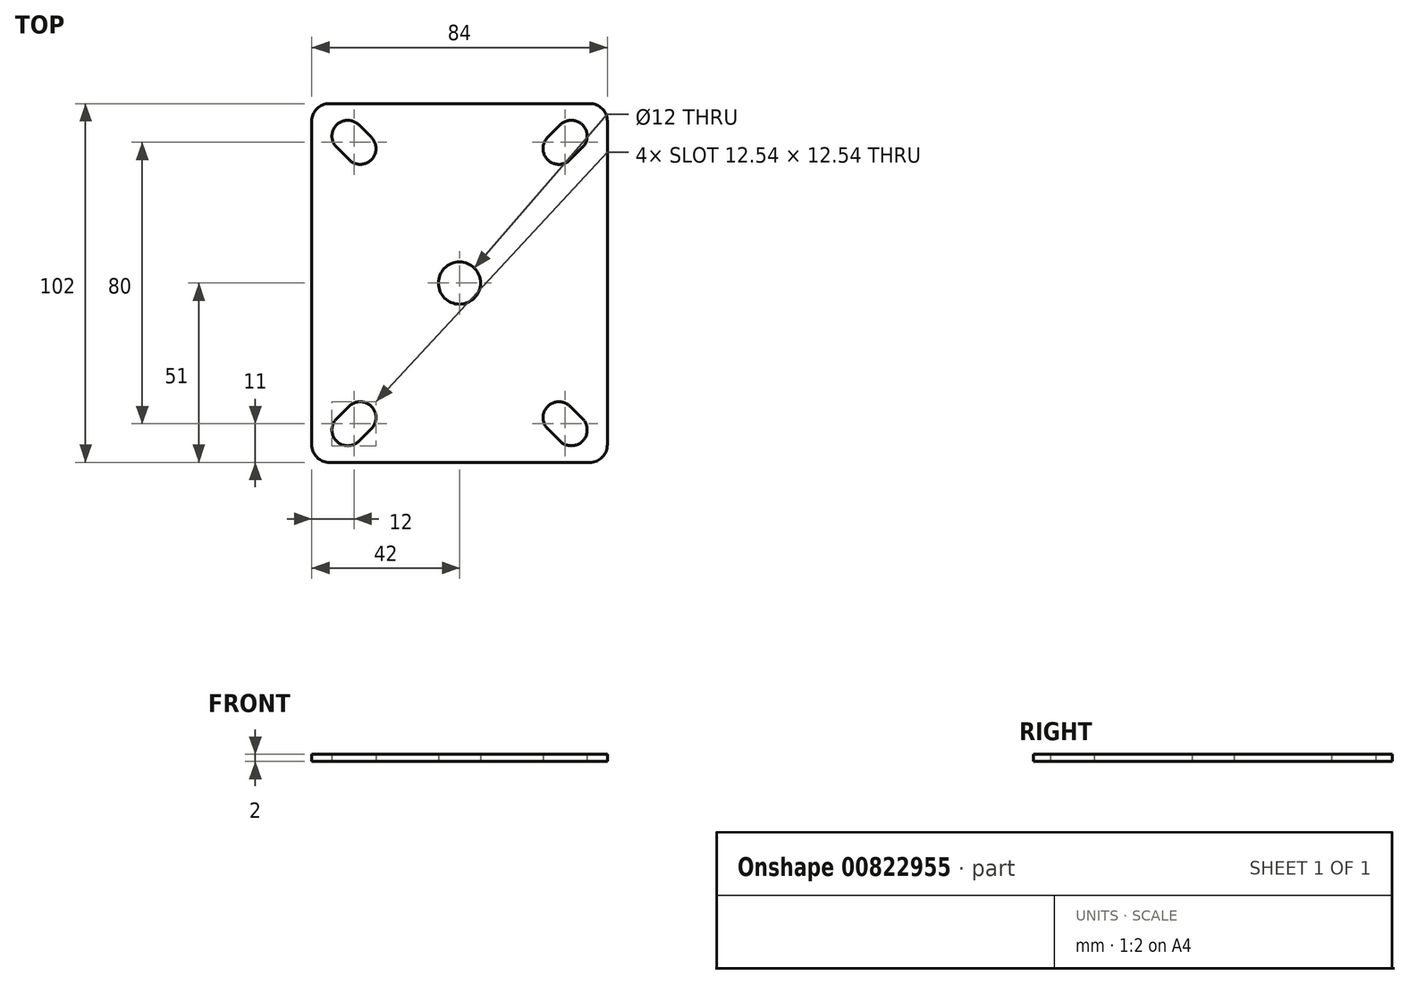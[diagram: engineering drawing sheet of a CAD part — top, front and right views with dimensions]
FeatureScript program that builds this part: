
annotation { "Feature Type Name" : "Feature", "Feature Type Description" : "" }
export const myFeature = defineFeature(function(context is Context, id is Id, definition is map)
    precondition{}
    {
        {
            var Q0;
            Q0=qCreatedBy(makeId("Top.planeOp"),FACE);
            var sketch = newSketch(context, id + "F0", { "sketchPlane" : qUnion([Q0])});
            skLineSegment(sketch, "E0.bottom", {"start": v(-42, -51) * mm, "end": v(42, -51) * mm});
            skLineSegment(sketch, "E0.top", {"start": v(-42, 51) * mm, "end": v(42, 51) * mm});
            skLineSegment(sketch, "E0.left", {"start": v(-42, -51) * mm, "end": v(-42, 51) * mm});
            skLineSegment(sketch, "E0.right", {"start": v(42, -51) * mm, "end": v(42, 51) * mm});
            skPoint(sketch, "E0.middle", {"position": v(0, 0) * mm});
            skLineSegment(sketch, "E1.bottom", {"start": v(-30, -40) * mm, "end": v(30, -40) * mm, "construction": true});
            skLineSegment(sketch, "E1.top", {"start": v(-30, 40) * mm, "end": v(30, 40) * mm, "construction": true});
            skLineSegment(sketch, "E1.left", {"start": v(-30, -40) * mm, "end": v(-30, 40) * mm, "construction": true});
            skLineSegment(sketch, "E1.right", {"start": v(30, -40) * mm, "end": v(30, 40) * mm, "construction": true});
            skLineSegment(sketch, "E2.0", {"start": v(-25.05, 35.05) * mm, "end": v(25.05, 35.05) * mm, "construction": true});
            skLineSegment(sketch, "E2.1", {"start": v(-25.05, -35.05) * mm, "end": v(-25.05, 35.05) * mm, "construction": true});
            skLineSegment(sketch, "E2.2", {"start": v(-25.05, -35.05) * mm, "end": v(25.05, -35.05) * mm, "construction": true});
            skLineSegment(sketch, "E2.3", {"start": v(25.05, -35.05) * mm, "end": v(25.05, 35.05) * mm, "construction": true});
            skLineSegment(sketch, "E3.0", {"start": v(-34.95, 44.95) * mm, "end": v(34.95, 44.95) * mm, "construction": true});
            skLineSegment(sketch, "E3.1", {"start": v(-34.95, -44.95) * mm, "end": v(-34.95, 44.95) * mm, "construction": true});
            skLineSegment(sketch, "E3.2", {"start": v(-34.95, -44.95) * mm, "end": v(34.95, -44.95) * mm, "construction": true});
            skLineSegment(sketch, "E3.3", {"start": v(34.95, -44.95) * mm, "end": v(34.95, 44.95) * mm, "construction": true});
            skLineSegment(sketch, "E4", {"start": v(-34.95, 44.95) * mm, "end": v(-25.05, 35.05) * mm, "construction": true});
            skLineSegment(sketch, "E5", {"start": v(-34.95, -44.95) * mm, "end": v(-25.05, -35.05) * mm, "construction": true});
            skLineSegment(sketch, "E6", {"start": v(34.95, -44.95) * mm, "end": v(25.05, -35.05) * mm, "construction": true});
            skLineSegment(sketch, "E7", {"start": v(25.05, 35.05) * mm, "end": v(34.95, 44.95) * mm, "construction": true});
            skLineSegment(sketch, "E8.0", {"start": v(-28.59, 44.95) * mm, "end": v(-25.05, 41.41) * mm});
            skLineSegment(sketch, "E9.0", {"start": v(-34.95, 38.59) * mm, "end": v(-31.41, 35.05) * mm});
            skLineSegment(sketch, "E10", {"start": v(-34.95, 44.95) * mm, "end": v(-31.77, 41.77) * mm, "construction": true});
            skLineSegment(sketch, "E11", {"start": v(-25.05, 35.05) * mm, "end": v(-28.23, 38.23) * mm, "construction": true});
            skArc(sketch, "E12", {"start": v(-31.41, 35.05) * mm, "mid": v(-25.05, 35.05) * mm, "end": v(-25.05, 41.41) * mm});
            skArc(sketch, "E13.trimOffspring", {"start": v(-28.59, 44.95) * mm, "mid": v(-34.95, 44.95) * mm, "end": v(-34.95, 38.59) * mm});
            skLineSegment(sketch, "E14", {"start": v(-30, 0) * mm, "end": v(30, 0) * mm, "construction": true});
            skLineSegment(sketch, "E15", {"start": v(0, 40) * mm, "end": v(0, -40) * mm, "construction": true});
            skLineSegment(sketch, "E16.MirrorCS", {"start": v(28.59, 44.95) * mm, "end": v(25.05, 41.41) * mm});
            skLineSegment(sketch, "E17.MirrorCS", {"start": v(34.95, 38.59) * mm, "end": v(31.41, 35.05) * mm});
            skArc(sketch, "E18.MirrorCS", {"start": v(31.41, 35.05) * mm, "mid": v(25.05, 35.05) * mm, "end": v(25.05, 41.41) * mm});
            skArc(sketch, "E19.MirrorCS", {"start": v(28.59, 44.95) * mm, "mid": v(34.95, 44.95) * mm, "end": v(34.95, 38.59) * mm});
            skArc(sketch, "E20.MirrorCS", {"start": v(31.41, -35.05) * mm, "mid": v(25.05, -35.05) * mm, "end": v(25.05, -41.41) * mm});
            skArc(sketch, "E21.MirrorCS", {"start": v(28.59, -44.95) * mm, "mid": v(34.95, -44.95) * mm, "end": v(34.95, -38.59) * mm});
            skArc(sketch, "E22.MirrorCS", {"start": v(-28.59, -44.95) * mm, "mid": v(-34.95, -44.95) * mm, "end": v(-34.95, -38.59) * mm});
            skArc(sketch, "E23.MirrorCS", {"start": v(-31.41, -35.05) * mm, "mid": v(-25.05, -35.05) * mm, "end": v(-25.05, -41.41) * mm});
            skLineSegment(sketch, "E24.MirrorCS", {"start": v(-28.59, -44.95) * mm, "end": v(-25.05, -41.41) * mm});
            skLineSegment(sketch, "E25.MirrorCS", {"start": v(-34.95, -38.59) * mm, "end": v(-31.41, -35.05) * mm});
            skLineSegment(sketch, "E26.MirrorCS", {"start": v(28.59, -44.95) * mm, "end": v(25.05, -41.41) * mm});
            skLineSegment(sketch, "E27.MirrorCS", {"start": v(34.95, -38.59) * mm, "end": v(31.41, -35.05) * mm});
            skCircle(sketch, "E28", {"center": v(0, 0) * mm, "radius": 6 * mm});
            skSolve(sketch);
        }
        {
            var Q0;
            Q0 = qSketchRegion(id + "F0", true);
            extrude(context, id + "F1", {"entities" : qUnion([Q0]), "depth" : 2 * mm, "offsetDistance" : 25 * mm});
        }
        {
            var Q0;
            Q0=makeQuery(id+"F1.opExtrude","SWEPT_EDGE",EDGE,{"disambiguationData":[OSD([sQuery(id+"F0.wireOp",EDGE,"E0.bottom"),sQuery(id+"F0.wireOp",EDGE,"E0.right")])]});
            var Q1;
            Q1=makeQuery(id+"F1.opExtrude","SWEPT_EDGE",EDGE,{"disambiguationData":[OSD([sQuery(id+"F0.wireOp",EDGE,"E0.top"),sQuery(id+"F0.wireOp",EDGE,"E0.right")])]});
            var Q2;
            Q2=makeQuery(id+"F1.opExtrude","SWEPT_EDGE",EDGE,{"disambiguationData":[OSD([sQuery(id+"F0.wireOp",EDGE,"E0.bottom"),sQuery(id+"F0.wireOp",EDGE,"E0.left")])]});
            var Q3;
            Q3=makeQuery(id+"F1.opExtrude","SWEPT_EDGE",EDGE,{"disambiguationData":[OSD([sQuery(id+"F0.wireOp",EDGE,"E0.top"),sQuery(id+"F0.wireOp",EDGE,"E0.left")])]});
            fillet(context, id + "F2", {"entities" : qUnion([Q0, Q1, Q2, Q3]), "radius" : 5 * mm, "tangentPropagation" : true, "allowEdgeOverflow" : false});
        }
    });
